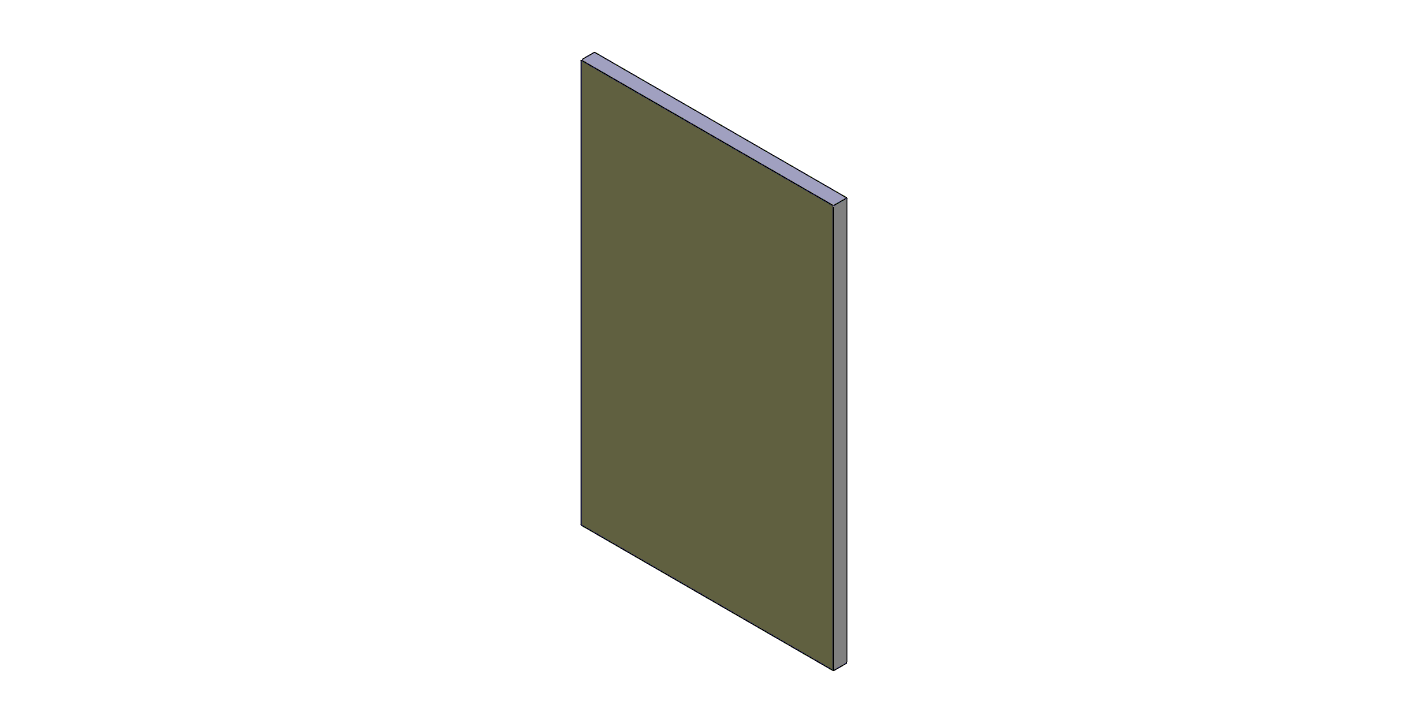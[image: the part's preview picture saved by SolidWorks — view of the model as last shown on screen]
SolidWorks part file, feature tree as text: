
SOLIDWORKS PART (.sldprt)
format: sldprt  version: not decoded by parser v0  size: 155,648 bytes
history: native  units: mm
features: sketch x4, cut_extrude x3, material x1, plane x1, extrude x1 (+11 scaffold rows collapsed)
feature tree (21):
  scaffold x11  (default folders/planes/origin — collapsed)
  material  "Material <not specified>"
  plane  "Plane1"  Offset=0mm
  sketch  "Sketch1"
  extrude  "Boss-Extrude1"  Depth=6.35mm
  sketch  "Sketch2"  dims[D1=3.2639mm]
  cut_extrude  "Cut-Extrude1"  Depth=6.35mm
  sketch  "Sketch3"  dims[D1=~4.944119mm]
  cut_extrude  "Cut-Extrude2"  Depth=9.525mm
  sketch  "Sketch4"  dims[D1=~4.80481mm]
  cut_extrude  "Cut-Extrude3"  Depth=9.525mm
decode coverage: 7 of 8 modeling features carry decoded parameters
note: ~ marks probable driven/reference dimensions
note: suppression state not decoded; provenance and decode notes live in map.json
